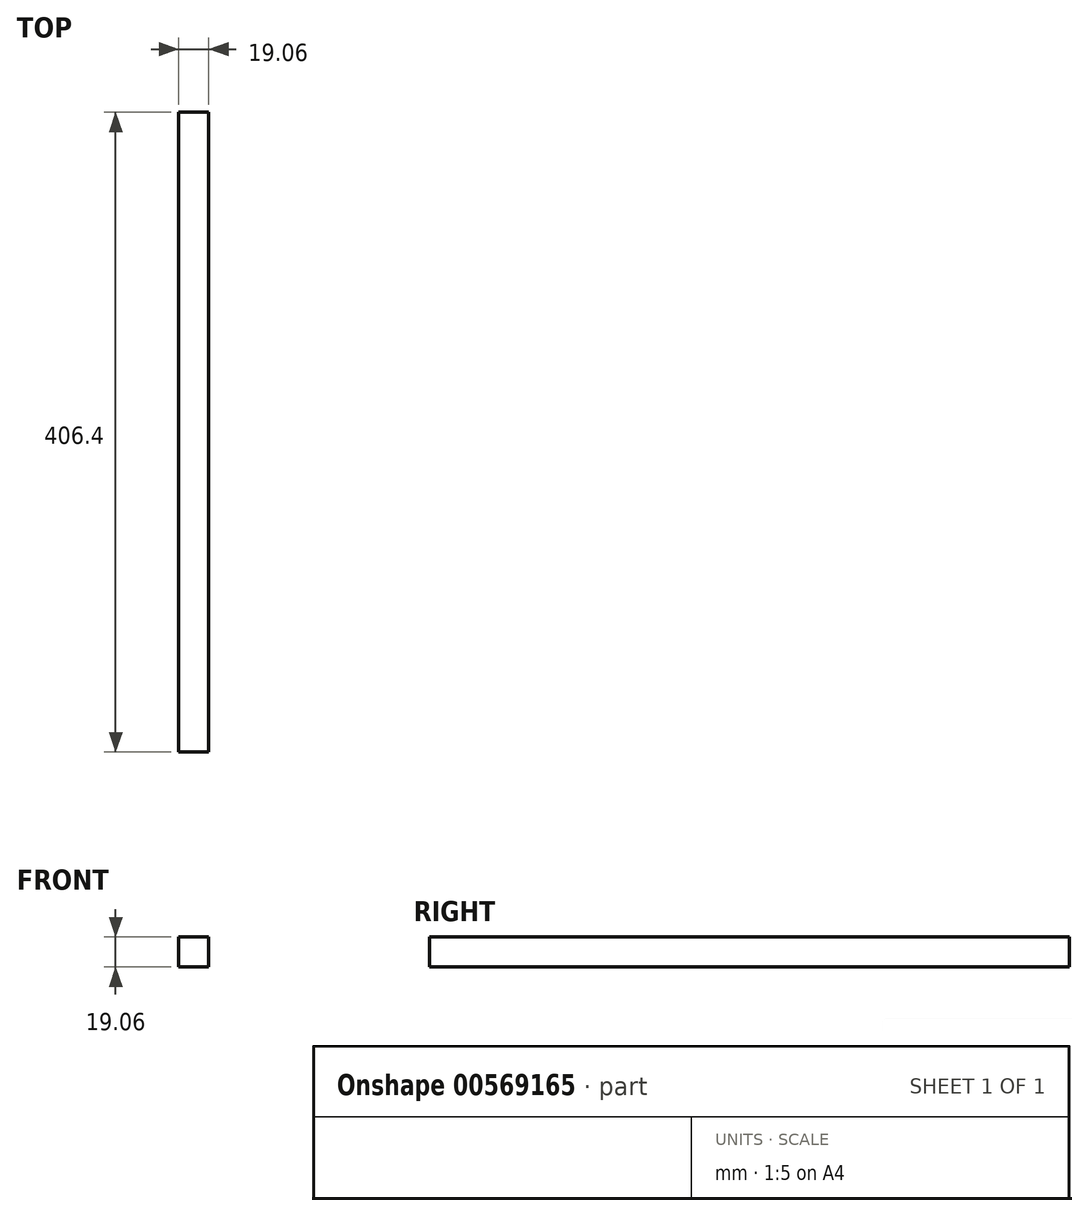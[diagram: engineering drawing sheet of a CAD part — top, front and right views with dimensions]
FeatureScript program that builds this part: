
annotation { "Feature Type Name" : "Feature", "Feature Type Description" : "" }
export const myFeature = defineFeature(function(context is Context, id is Id, definition is map)
    precondition{}
    {
        {
            var Q0;
            Q0=qCreatedBy(makeId("Top.planeOp"),FACE);
            var sketch = newSketch(context, id + "F0", { "sketchPlane" : qUnion([Q0])});
            skLineSegment(sketch, "E0.bottom", {"start": v(-9.53, 203.2) * mm, "end": v(9.52, 203.2) * mm});
            skLineSegment(sketch, "E0.top", {"start": v(-9.53, -203.2) * mm, "end": v(9.52, -203.2) * mm});
            skLineSegment(sketch, "E0.left", {"start": v(-9.53, 203.2) * mm, "end": v(-9.53, -203.2) * mm});
            skLineSegment(sketch, "E0.right", {"start": v(9.52, 203.2) * mm, "end": v(9.52, -203.2) * mm});
            skPoint(sketch, "E0.middle", {"position": v(0, 0) * mm});
            skSolve(sketch);
        }
        {
            var Q0;
            Q0=makeQuery(id+"F0.imprint","IMPRINT",FACE,{"disambiguationData":[TD([[makeQuery(id+"F0.imprint","IMPRINT",EDGE,{"derivedFrom":sQuery(id+"F0.wireOp",EDGE,"E0.bottom")}),-1.0]])]});
            extrude(context, id + "F1", {"entities" : qUnion([Q0]), "endBound" : BoundingType.SYMMETRIC, "depth" : 19.05 * mm, "offsetDistance" : 25.4 * mm});
        }
    });
